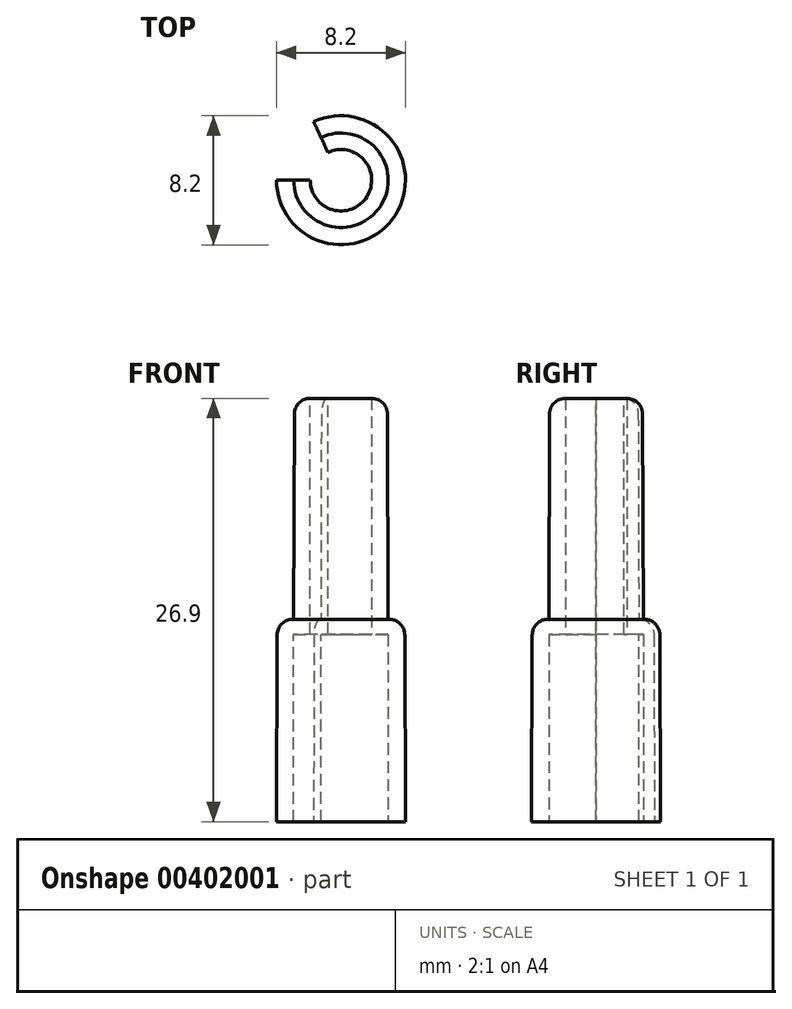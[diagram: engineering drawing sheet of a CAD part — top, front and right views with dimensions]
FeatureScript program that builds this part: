
annotation { "Feature Type Name" : "Feature", "Feature Type Description" : "" }
export const myFeature = defineFeature(function(context is Context, id is Id, definition is map)
    precondition{}
    {
        {
            var Q0;
            Q0=qCreatedBy(makeId("Front.planeOp"),FACE);
            var sketch = newSketch(context, id + "F0", { "sketchPlane" : qUnion([Q0])});
            skLineSegment(sketch, "E0", {"start": v(0, 0) * mm, "end": v(0, 24.03) * mm, "construction": true});
            skLineSegment(sketch, "E1", {"start": v(-3, 0) * mm, "end": v(-3, 11.9) * mm});
            skLineSegment(sketch, "E2", {"start": v(-3, 11.9) * mm, "end": v(-1.95, 11.9) * mm});
            skLineSegment(sketch, "E3", {"start": v(-1.95, 11.9) * mm, "end": v(-1.95, 26.9) * mm});
            skLineSegment(sketch, "E4", {"start": v(-1.95, 26.9) * mm, "end": v(-2.95, 26.9) * mm});
            skLineSegment(sketch, "E5", {"start": v(-2.95, 26.9) * mm, "end": v(-3, 12.87) * mm});
            skLineSegment(sketch, "E6", {"start": v(-3, 12.87) * mm, "end": v(-4.05, 12.87) * mm});
            skLineSegment(sketch, "E7", {"start": v(-4.05, 12.87) * mm, "end": v(-4.1, 0) * mm});
            skLineSegment(sketch, "E8", {"start": v(-4.1, 0) * mm, "end": v(-3, 0) * mm});
            skSolve(sketch);
        }
        {
            var Q0;
            Q0 = qSketchRegion(id + "F0", true);
            var Q1;
            Q1=sQuery(id+"F0.wireOp",EDGE,"E0");
            revolve(context, id + "F1", {"entities" : qUnion([Q0]), "axis" : qUnion([Q1]), "revolveType" : RevolveType.ONE_DIRECTION, "angle" : 295 * degree});
        }
        {
            var Q0;
            Q0=makeQuery(id+"F1.opRevolve","SWEPT_EDGE",EDGE,{"disambiguationData":[OSD([sQuery(id+"F0.wireOp",EDGE,"E4"),sQuery(id+"F0.wireOp",EDGE,"E5")])]});
            var Q1;
            Q1=makeQuery(id+"F1.opRevolve","SWEPT_EDGE",EDGE,{"disambiguationData":[OSD([sQuery(id+"F0.wireOp",EDGE,"E6"),sQuery(id+"F0.wireOp",EDGE,"E7")])]});
            fillet(context, id + "F2", {"entities" : qUnion([Q0, Q1]), "radius" : 1 * mm, "tangentPropagation" : true, "allowEdgeOverflow" : false});
        }
    });
